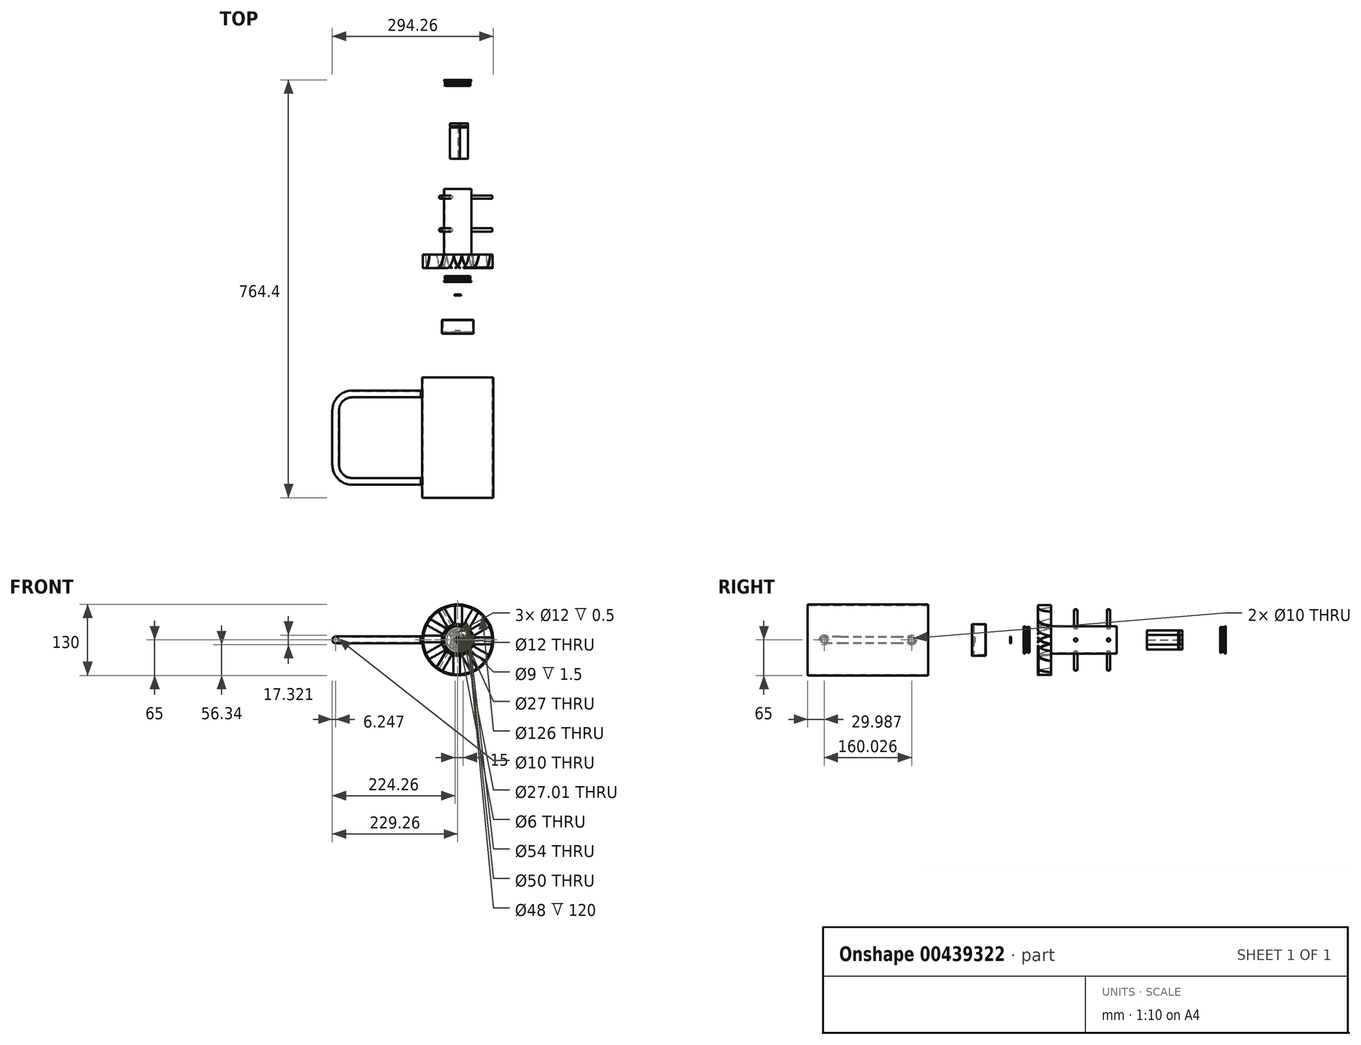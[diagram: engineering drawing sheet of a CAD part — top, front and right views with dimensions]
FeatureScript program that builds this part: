
annotation { "Feature Type Name" : "Feature", "Feature Type Description" : "" }
export const myFeature = defineFeature(function(context is Context, id is Id, definition is map)
    precondition{}
    {
        {
            var Q0;
            Q0=qCreatedBy(makeId("Right.planeOp"),FACE);
            var sketch = newSketch(context, id + "F0", { "sketchPlane" : qUnion([Q0])});
            skLineSegment(sketch, "E0", {"start": v(0, 0) * mm, "end": v(0, 5.8) * mm});
            skLineSegment(sketch, "E1", {"start": v(0.2, 6) * mm, "end": v(2, 6) * mm});
            skLineSegment(sketch, "E2", {"start": v(2, 6) * mm, "end": v(2, 4.31) * mm});
            skLineSegment(sketch, "E3", {"start": v(1.68, 3.67) * mm, "end": v(0.77, 3) * mm});
            skLineSegment(sketch, "E4", {"start": v(0.77, 3) * mm, "end": v(0.46, 3.46) * mm});
            skLineSegment(sketch, "E5", {"start": v(0.46, 3.46) * mm, "end": v(0.97, 4.13) * mm});
            skLineSegment(sketch, "E6", {"start": v(0.81, 4.53) * mm, "end": v(0, 4.66) * mm});
            skArc(sketch, "E7.filletArc", {"start": v(0.97, 4.13) * mm, "mid": v(1, 4.38) * mm, "end": v(0.81, 4.53) * mm});
            skPoint(sketch, "E8.visualSharp", {"position": v(0, 6) * mm});
            skArc(sketch, "E8.filletArc", {"start": v(0.2, 6) * mm, "mid": v(0.06, 5.94) * mm, "end": v(0, 5.8) * mm});
            skPoint(sketch, "E9.visualSharp", {"position": v(2, 3.9) * mm});
            skArc(sketch, "E9.filletArc", {"start": v(1.68, 3.67) * mm, "mid": v(1.91, 3.95) * mm, "end": v(2, 4.31) * mm});
            skLineSegment(sketch, "E10", {"start": v(-2.35, 0) * mm, "end": v(5.53, 0) * mm, "construction": true});
            skSolve(sketch);
        }
        {
            var Q0;
            Q0 = qSketchRegion(id + "F0", true);
            var Q1;
            Q1=sQuery(id+"F0.wireOp",EDGE,"E10");
            revolve(context, id + "F1", {"entities" : qUnion([Q0]), "axis" : qUnion([Q1]), "revolveType" : RevolveType.FULL});
        }
        {
            var Q0;
            Q0=makeQuery(id+"F1.opRevolve","SWEPT_BODY",BODY,{"disambiguationData":[OSD([sQuery(id+"F0.wireOp",EDGE,"E0"),sQuery(id+"F0.wireOp",EDGE,"E1"),sQuery(id+"F0.wireOp",EDGE,"E2"),sQuery(id+"F0.wireOp",EDGE,"E3"),sQuery(id+"F0.wireOp",EDGE,"E4"),sQuery(id+"F0.wireOp",EDGE,"E5"),sQuery(id+"F0.wireOp",EDGE,"E6"),sQuery(id+"F0.wireOp",EDGE,"E7.filletArc"),sQuery(id+"F0.wireOp",EDGE,"E8.filletArc"),sQuery(id+"F0.wireOp",EDGE,"E9.filletArc")])]});
            var Q1;
            Q1=makeQuery(id+"F1.opRevolve","SWEPT_FACE",FACE,{"disambiguationData":[OSD([sQuery(id+"F0.wireOp",EDGE,"E1")])]});
            transform(context, id + "F2", {"entities" : qUnion([Q0]), "transformType" : TransformType.TRANSLATION_DISTANCE, "transformDirection" : qUnion([Q1]), "distance" : 50 * mm, "makeCopy" : false});
        }
        {
            var Q0;
            Q0=qCreatedBy(makeId("Right.planeOp"),FACE);
            var sketch = newSketch(context, id + "F3", { "sketchPlane" : qUnion([Q0])});
            skLineSegment(sketch, "E11", {"start": v(0, 0) * mm, "end": v(0, 25) * mm});
            skLineSegment(sketch, "E12", {"start": v(0, 25) * mm, "end": v(2, 25) * mm});
            skLineSegment(sketch, "E13", {"start": v(2, 25) * mm, "end": v(2, 23.5) * mm});
            skLineSegment(sketch, "E14", {"start": v(2, 23.5) * mm, "end": v(4, 23.5) * mm});
            skLineSegment(sketch, "E15", {"start": v(4, 23.5) * mm, "end": v(4, 20) * mm});
            skLineSegment(sketch, "E16", {"start": v(4, 20) * mm, "end": v(7.5, 20) * mm});
            skLineSegment(sketch, "E17", {"start": v(7.5, 20) * mm, "end": v(7.5, 23.5) * mm});
            skLineSegment(sketch, "E18", {"start": v(7.5, 23.5) * mm, "end": v(10.5, 23.5) * mm});
            skLineSegment(sketch, "E19", {"start": v(10.5, 23.5) * mm, "end": v(10.5, 13.5) * mm});
            skLineSegment(sketch, "E20", {"start": v(10.5, 13.5) * mm, "end": v(4, 13.5) * mm});
            skLineSegment(sketch, "E21", {"start": v(4, 13.5) * mm, "end": v(4, 4.5) * mm});
            skLineSegment(sketch, "E22", {"start": v(4, 4.5) * mm, "end": v(2.5, 4.5) * mm});
            skLineSegment(sketch, "E23", {"start": v(2.5, 4.5) * mm, "end": v(2.5, 6) * mm});
            skLineSegment(sketch, "E24", {"start": v(2.5, 6) * mm, "end": v(0, 6) * mm});
            skLineSegment(sketch, "E25", {"start": v(-5.31, 0) * mm, "end": v(25.38, 0) * mm, "construction": true});
            skSolve(sketch);
        }
        {
            var Q0;
            Q0 = qSketchRegion(id + "F3", true);
            var Q1;
            Q1=sQuery(id+"F3.wireOp",EDGE,"E25");
            revolve(context, id + "F4", {"entities" : qUnion([Q0]), "axis" : qUnion([Q1]), "revolveType" : RevolveType.FULL});
        }
        {
            var Q0;
            Q0=makeQuery(id+"F4.opRevolve","SWEPT_EDGE",EDGE,{"disambiguationData":[OSD([sQuery(id+"F3.wireOp",EDGE,"E11"),sQuery(id+"F3.wireOp",EDGE,"E24")])]});
            chamfer(context, id + "F5", {"entities" : qUnion([Q0]), "chamferType" : ChamferType.OFFSET_ANGLE, "width" : .5 * mm, "oppositeDirection" : false, "angle" : 30 * degree, "tangentPropagation" : true});
        }
        {
            var Q0;
            Q0=makeQuery(id+"F4.opRevolve","SWEPT_EDGE",EDGE,{"disambiguationData":[OSD([sQuery(id+"F3.wireOp",EDGE,"E23"),sQuery(id+"F3.wireOp",EDGE,"E24")])]});
            var Q1;
            Q1=makeQuery(id+"F4.opRevolve","SWEPT_EDGE",EDGE,{"disambiguationData":[OSD([sQuery(id+"F3.wireOp",EDGE,"E17"),sQuery(id+"F3.wireOp",EDGE,"E18")])]});
            var Q2;
            Q2=makeQuery(id+"F4.opRevolve","SWEPT_EDGE",EDGE,{"disambiguationData":[OSD([sQuery(id+"F3.wireOp",EDGE,"E15"),sQuery(id+"F3.wireOp",EDGE,"E16")])]});
            var Q3;
            Q3=makeQuery(id+"F4.opRevolve","SWEPT_EDGE",EDGE,{"disambiguationData":[OSD([sQuery(id+"F3.wireOp",EDGE,"E20"),sQuery(id+"F3.wireOp",EDGE,"E21")])]});
            fillet(context, id + "F6", {"entities" : qUnion([Q0, Q1, Q2, Q3]), "radius" : .3 * mm, "tangentPropagation" : true, "allowEdgeOverflow" : false});
        }
        {
            var Q0;
            Q0=makeQuery(id+"F4.opRevolve","SWEPT_EDGE",EDGE,{"disambiguationData":[OSD([sQuery(id+"F3.wireOp",EDGE,"E11"),sQuery(id+"F3.wireOp",EDGE,"E12")])]});
            var Q1;
            Q1=makeQuery(id+"F4.opRevolve","SWEPT_EDGE",EDGE,{"disambiguationData":[OSD([sQuery(id+"F3.wireOp",EDGE,"E12"),sQuery(id+"F3.wireOp",EDGE,"E13")])]});
            var Q2;
            Q2=makeQuery(id+"F4.opRevolve","SWEPT_EDGE",EDGE,{"disambiguationData":[OSD([sQuery(id+"F3.wireOp",EDGE,"E14"),sQuery(id+"F3.wireOp",EDGE,"E15")])]});
            var Q3;
            Q3=makeQuery(id+"F4.opRevolve","SWEPT_EDGE",EDGE,{"disambiguationData":[OSD([sQuery(id+"F3.wireOp",EDGE,"E17"),sQuery(id+"F3.wireOp",EDGE,"E18")])]});
            var Q4;
            Q4=makeQuery(id+"F4.opRevolve","SWEPT_EDGE",EDGE,{"disambiguationData":[OSD([sQuery(id+"F3.wireOp",EDGE,"E18"),sQuery(id+"F3.wireOp",EDGE,"E19")])]});
            var Q5;
            Q5=makeQuery(id+"F4.opRevolve","SWEPT_EDGE",EDGE,{"disambiguationData":[OSD([sQuery(id+"F3.wireOp",EDGE,"E19"),sQuery(id+"F3.wireOp",EDGE,"E20")])]});
            chamfer(context, id + "F7", {"entities" : qUnion([Q0, Q1, Q2, Q3, Q4, Q5]), "width" : .5 * mm, "tangentPropagation" : true});
        }
        {
            var Q0;
            Q0=qCreatedBy(makeId("Right.planeOp"),FACE);
            var sketch = newSketch(context, id + "F8", { "sketchPlane" : qUnion([Q0])});
            skCircle(sketch, "E26", {"center": v(5.75, 21.75) * mm, "radius": 1.75 * mm});
            skLineSegment(sketch, "E27", {"start": v(-6.06, 0) * mm, "end": v(25.96, 0) * mm, "construction": true});
            skSolve(sketch);
        }
        {
            var Q0;
            Q0=makeQuery(id+"F8.imprint","IMPRINT",FACE,{"disambiguationData":[TD([[makeQuery(id+"F8.imprint","IMPRINT",EDGE,{"derivedFrom":sQuery(id+"F8.wireOp",EDGE,"E26")}),1.0]])]});
            var Q1;
            Q1=sQuery(id+"F8.wireOp",EDGE,"E27");
            revolve(context, id + "F9", {"operationType" : NewBodyOperationType.ADD, "entities" : qUnion([Q0]), "axis" : qUnion([Q1]), "revolveType" : RevolveType.FULL});
        }
        {
            var Q0;
            Q0=makeQuery(id+"F4.opRevolve","SWEPT_BODY",BODY,{"disambiguationData":[OSD([sQuery(id+"F3.wireOp",EDGE,"E11"),sQuery(id+"F3.wireOp",EDGE,"E12"),sQuery(id+"F3.wireOp",EDGE,"E13"),sQuery(id+"F3.wireOp",EDGE,"E14"),sQuery(id+"F3.wireOp",EDGE,"E15"),sQuery(id+"F3.wireOp",EDGE,"E16"),sQuery(id+"F3.wireOp",EDGE,"E17"),sQuery(id+"F3.wireOp",EDGE,"E18"),sQuery(id+"F3.wireOp",EDGE,"E19"),sQuery(id+"F3.wireOp",EDGE,"E20"),sQuery(id+"F3.wireOp",EDGE,"E21"),sQuery(id+"F3.wireOp",EDGE,"E22"),sQuery(id+"F3.wireOp",EDGE,"E23"),sQuery(id+"F3.wireOp",EDGE,"E24")])]});
            var Q1;
            Q1=makeQuery(id+"F9.opRevolve","SWEPT_BODY",BODY,{"disambiguationData":[OSD([sQuery(id+"F8.wireOp",EDGE,"E26")])]});
            var Q2;
            Q2=makeQuery(id+"F4.opRevolve","SWEPT_FACE",FACE,{"disambiguationData":[OSD([sQuery(id+"F3.wireOp",EDGE,"E18")])]});
            transform(context, id + "F10", {"entities" : qUnion([Q0, Q1]), "transformType" : TransformType.TRANSLATION_DISTANCE, "transformDirection" : qUnion([Q2]), "distance" : 25 * mm, "makeCopy" : false});
        }
        {
            var Q0;
            Q0=qCreatedBy(makeId("Right.planeOp"),FACE);
            var sketch = newSketch(context, id + "F11", { "sketchPlane" : qUnion([Q0])});
            skLineSegment(sketch, "E28", {"start": v(0, 3) * mm, "end": v(0, 5) * mm});
            skLineSegment(sketch, "E29", {"start": v(0, 5) * mm, "end": v(2, 5) * mm});
            skLineSegment(sketch, "E30", {"start": v(2, 5) * mm, "end": v(2, 25) * mm});
            skLineSegment(sketch, "E31", {"start": v(2, 25) * mm, "end": v(0, 25) * mm});
            skLineSegment(sketch, "E32", {"start": v(0, 25) * mm, "end": v(0, 29) * mm});
            skLineSegment(sketch, "E33", {"start": v(0, 29) * mm, "end": v(25.72, 29) * mm});
            skLineSegment(sketch, "E34", {"start": v(25.72, 29) * mm, "end": v(25.72, 27) * mm});
            skLineSegment(sketch, "E35", {"start": v(25.72, 27) * mm, "end": v(3.72, 27) * mm});
            skLineSegment(sketch, "E36", {"start": v(3.72, 27) * mm, "end": v(3.72, 5) * mm});
            skLineSegment(sketch, "E37", {"start": v(3.72, 5) * mm, "end": v(5.72, 5) * mm});
            skLineSegment(sketch, "E38", {"start": v(5.72, 5) * mm, "end": v(5.72, 3) * mm});
            skLineSegment(sketch, "E39", {"start": v(5.72, 3) * mm, "end": v(0, 3) * mm});
            skLineSegment(sketch, "E40", {"start": v(-6.87, 0) * mm, "end": v(43.92, 0) * mm, "construction": true});
            skSolve(sketch);
        }
        {
            var Q0;
            Q0 = qSketchRegion(id + "F11", true);
            var Q1;
            Q1=sQuery(id+"F11.wireOp",EDGE,"E40");
            revolve(context, id + "F12", {"entities" : qUnion([Q0]), "axis" : qUnion([Q1]), "revolveType" : RevolveType.FULL});
        }
        {
            var Q0;
            Q0=makeQuery(id+"F12.opRevolve","SWEPT_EDGE",EDGE,{"disambiguationData":[OSD([sQuery(id+"F11.wireOp",EDGE,"E28"),sQuery(id+"F11.wireOp",EDGE,"E39")])]});
            var Q1;
            Q1=makeQuery(id+"F12.opRevolve","SWEPT_EDGE",EDGE,{"disambiguationData":[OSD([sQuery(id+"F11.wireOp",EDGE,"E28"),sQuery(id+"F11.wireOp",EDGE,"E29")])]});
            var Q2;
            Q2=makeQuery(id+"F12.opRevolve","SWEPT_EDGE",EDGE,{"disambiguationData":[OSD([sQuery(id+"F11.wireOp",EDGE,"E31"),sQuery(id+"F11.wireOp",EDGE,"E32")])]});
            var Q3;
            Q3=makeQuery(id+"F12.opRevolve","SWEPT_EDGE",EDGE,{"disambiguationData":[OSD([sQuery(id+"F11.wireOp",EDGE,"E32"),sQuery(id+"F11.wireOp",EDGE,"E33")])]});
            var Q4;
            Q4=makeQuery(id+"F12.opRevolve","SWEPT_EDGE",EDGE,{"disambiguationData":[OSD([sQuery(id+"F11.wireOp",EDGE,"E33"),sQuery(id+"F11.wireOp",EDGE,"E34")])]});
            var Q5;
            Q5=makeQuery(id+"F12.opRevolve","SWEPT_EDGE",EDGE,{"disambiguationData":[OSD([sQuery(id+"F11.wireOp",EDGE,"E34"),sQuery(id+"F11.wireOp",EDGE,"E35")])]});
            var Q6;
            Q6=makeQuery(id+"F12.opRevolve","SWEPT_EDGE",EDGE,{"disambiguationData":[OSD([sQuery(id+"F11.wireOp",EDGE,"E37"),sQuery(id+"F11.wireOp",EDGE,"E38")])]});
            var Q7;
            Q7=makeQuery(id+"F12.opRevolve","SWEPT_EDGE",EDGE,{"disambiguationData":[OSD([sQuery(id+"F11.wireOp",EDGE,"E38"),sQuery(id+"F11.wireOp",EDGE,"E39")])]});
            chamfer(context, id + "F13", {"entities" : qUnion([Q0, Q1, Q2, Q3, Q4, Q5, Q6, Q7]), "width" : .5 * mm, "tangentPropagation" : true});
        }
        {
            var Q0;
            Q0=makeQuery(id+"F12.opRevolve","SWEPT_EDGE",EDGE,{"disambiguationData":[OSD([sQuery(id+"F11.wireOp",EDGE,"E29"),sQuery(id+"F11.wireOp",EDGE,"E30")])]});
            var Q1;
            Q1=makeQuery(id+"F12.opRevolve","SWEPT_EDGE",EDGE,{"disambiguationData":[OSD([sQuery(id+"F11.wireOp",EDGE,"E30"),sQuery(id+"F11.wireOp",EDGE,"E31")])]});
            var Q2;
            Q2=makeQuery(id+"F12.opRevolve","SWEPT_EDGE",EDGE,{"disambiguationData":[OSD([sQuery(id+"F11.wireOp",EDGE,"E35"),sQuery(id+"F11.wireOp",EDGE,"E36")])]});
            var Q3;
            Q3=makeQuery(id+"F12.opRevolve","SWEPT_EDGE",EDGE,{"disambiguationData":[OSD([sQuery(id+"F11.wireOp",EDGE,"E36"),sQuery(id+"F11.wireOp",EDGE,"E37")])]});
            fillet(context, id + "F14", {"entities" : qUnion([Q0, Q1, Q2, Q3]), "radius" : 1 * mm, "tangentPropagation" : true, "allowEdgeOverflow" : false});
        }
        {
            var Q0;
            Q0=qCreatedBy(makeId("Right.planeOp"),FACE);
            cPlane(context, id + "F15", {"entities" : qUnion([Q0]), "cplaneType" : CPlaneType.OFFSET, "offset" : 29 * mm, "width" : 150 * mm, "height" : 150 * mm});
        }
        {
            var Q0;
            Q0=qCreatedBy(id+"F15.planeOp",FACE);
            var sketch = newSketch(context, id + "F16", { "sketchPlane" : qUnion([Q0])});
            skFitSpline(sketch, "E41", {"points": [v(1.8, 4) * mm, v(0.76, 4.47) * mm, v(0.51, 3.63) * mm, v(0.79, 2.55) * mm, v(4.93, -1.3) * mm, v(11.9, -4.72) * mm, v(18.63, -6.73) * mm, v(25, -7.85) * mm], "startDerivative": vector(-10.22, 8.26) * mm, "endDerivative": vector(8.4, -0.71) * mm});
            skFitSpline(sketch, "E42", {"points": [v(25, -7.85) * mm, v(25.14, -7.8) * mm, v(24.7, -7.38) * mm, v(23.01, -6.96) * mm, v(19.16, -6.12) * mm, v(12.02, -3.74) * mm, v(5.67, -0.3) * mm, v(3.11, 2.55) * mm, v(1.8, 4) * mm], "startDerivative": vector(9.33, 0.6) * mm, "endDerivative": vector(-14.15, 14.4) * mm});
            skSolve(sketch);
        }
        {
            var Q0;
            Q0 = qSketchRegion(id + "F16", true);
            extrude(context, id + "F17", {"entities" : qUnion([Q0]), "depth" : 35 * mm, "hasSecondDirection" : true, "secondDirectionOppositeDirection" : true, "secondDirectionDepth" : 1.6 * mm});
        }
        {
            var Q0;
            Q0=makeQuery(id+"F12.opRevolve","SWEPT_BODY",BODY,{"disambiguationData":[OSD([sQuery(id+"F11.wireOp",EDGE,"E28"),sQuery(id+"F11.wireOp",EDGE,"E29"),sQuery(id+"F11.wireOp",EDGE,"E30"),sQuery(id+"F11.wireOp",EDGE,"E31"),sQuery(id+"F11.wireOp",EDGE,"E32"),sQuery(id+"F11.wireOp",EDGE,"E33"),sQuery(id+"F11.wireOp",EDGE,"E34"),sQuery(id+"F11.wireOp",EDGE,"E35"),sQuery(id+"F11.wireOp",EDGE,"E36"),sQuery(id+"F11.wireOp",EDGE,"E37"),sQuery(id+"F11.wireOp",EDGE,"E38"),sQuery(id+"F11.wireOp",EDGE,"E39")])]});
            var Q1;
            Q1=makeQuery(id+"F17.opExtrude","SWEPT_BODY",BODY,{"disambiguationData":[OSD([sQuery(id+"F16.wireOp",EDGE,"E41"),sQuery(id+"F16.wireOp",EDGE,"E42")])]});
            booleanBodies(context, id + "F18", {"operationType" : BooleanOperationType.SUBTRACTION, "tools" : qUnion([Q0]), "targets" : qUnion([Q1]), "keepTools" : true});
        }
        {
            var Q0;
            Q0=makeQuery(id+"F17.opExtrude","SWEPT_BODY",BODY,{"disambiguationData":[OSD([sQuery(id+"F16.wireOp",EDGE,"E41"),sQuery(id+"F16.wireOp",EDGE,"E42")])]});
            var Q1;
            Q1=makeQuery(id+"F12.opRevolve","SWEPT_FACE",FACE,{"disambiguationData":[OSD([sQuery(id+"F11.wireOp",EDGE,"E33")])]});
            circularPattern(context, id + "F19", {"entities" : qUnion([Q0]), "axis" : qUnion([Q1]), "angle" : 360 * degree, "instanceCount" : 12, "equalSpace" : true});
        }
        {
            var Q0;
            Q0=makeQuery(id+"F12.opRevolve","SWEPT_BODY",BODY,{"disambiguationData":[OSD([sQuery(id+"F11.wireOp",EDGE,"E28"),sQuery(id+"F11.wireOp",EDGE,"E29"),sQuery(id+"F11.wireOp",EDGE,"E30"),sQuery(id+"F11.wireOp",EDGE,"E31"),sQuery(id+"F11.wireOp",EDGE,"E32"),sQuery(id+"F11.wireOp",EDGE,"E33"),sQuery(id+"F11.wireOp",EDGE,"E34"),sQuery(id+"F11.wireOp",EDGE,"E35"),sQuery(id+"F11.wireOp",EDGE,"E36"),sQuery(id+"F11.wireOp",EDGE,"E37"),sQuery(id+"F11.wireOp",EDGE,"E38"),sQuery(id+"F11.wireOp",EDGE,"E39")])]});
            var Q1;
            Q1=makeQuery(id+"F4.opRevolve","SWEPT_FACE",FACE,{"disambiguationData":[OSD([sQuery(id+"F3.wireOp",EDGE,"E18")])]});
            transform(context, id + "F20", {"entities" : qUnion([Q0]), "transformType" : TransformType.TRANSLATION_DISTANCE, "transformDirection" : qUnion([Q1]), "distance" : 120 * mm, "makeCopy" : false});
        }
        {
            var Q0;
            Q0=qCreatedBy(makeId("Front.planeOp"),FACE);
            var sketch = newSketch(context, id + "F21", { "sketchPlane" : qUnion([Q0])});
            skCircle(sketch, "E43", {"center": v(0, 0) * mm, "radius": 65 * mm});
            skCircle(sketch, "E44", {"center": v(0, 0) * mm, "radius": 63 * mm});
            skSolve(sketch);
        }
        {
            var Q0;
            Q0 = qSketchRegion(id + "F21", true);
            extrude(context, id + "F22", {"entities" : qUnion([Q0]), "depth" : 220 * mm});
        }
        {
            var Q0;
            Q0=makeQuery(id+"F22.opExtrude","CAP_EDGE",EDGE,{"disambiguationData":[OSD([sQuery(id+"F21.wireOp",EDGE,"E43")])],"isStart":false});
            var Q1;
            Q1=makeQuery(id+"F22.opExtrude","CAP_EDGE",EDGE,{"disambiguationData":[OSD([sQuery(id+"F21.wireOp",EDGE,"E44")])],"isStart":false});
            var Q2;
            Q2=makeQuery(id+"F22.opExtrude","CAP_EDGE",EDGE,{"disambiguationData":[OSD([sQuery(id+"F21.wireOp",EDGE,"E43")])],"isStart":true});
            var Q3;
            Q3=makeQuery(id+"F22.opExtrude","CAP_EDGE",EDGE,{"disambiguationData":[OSD([sQuery(id+"F21.wireOp",EDGE,"E44")])],"isStart":true});
            fillet(context, id + "F23", {"entities" : qUnion([Q0, Q1, Q2, Q3]), "radius" : 1 * mm, "tangentPropagation" : true, "allowEdgeOverflow" : false});
        }
        {
            var Q0;
            Q0=makeQuery(id+"F22.opExtrude","SWEPT_BODY",BODY,{"disambiguationData":[OSD([sQuery(id+"F21.wireOp",EDGE,"E43"),sQuery(id+"F21.wireOp",EDGE,"E44")])]});
            var Q1;
            Q1=makeQuery(id+"F12.opRevolve","SWEPT_BODY",BODY,{"disambiguationData":[OSD([sQuery(id+"F11.wireOp",EDGE,"E28"),sQuery(id+"F11.wireOp",EDGE,"E29"),sQuery(id+"F11.wireOp",EDGE,"E30"),sQuery(id+"F11.wireOp",EDGE,"E31"),sQuery(id+"F11.wireOp",EDGE,"E32"),sQuery(id+"F11.wireOp",EDGE,"E33"),sQuery(id+"F11.wireOp",EDGE,"E34"),sQuery(id+"F11.wireOp",EDGE,"E35"),sQuery(id+"F11.wireOp",EDGE,"E36"),sQuery(id+"F11.wireOp",EDGE,"E37"),sQuery(id+"F11.wireOp",EDGE,"E38"),sQuery(id+"F11.wireOp",EDGE,"E39")])]});
            booleanBodies(context, id + "F24", {"operationType" : BooleanOperationType.SUBTRACTION, "tools" : qUnion([Q0]), "targets" : qUnion([Q1]), "keepTools" : true});
        }
        {
            var Q0;
            Q0=makeQuery(id+"F22.opExtrude","SWEPT_BODY",BODY,{"disambiguationData":[OSD([sQuery(id+"F21.wireOp",EDGE,"E43"),sQuery(id+"F21.wireOp",EDGE,"E44")])]});
            var Q1;
            Q1=makeQuery(id+"F22.opExtrude","SWEPT_FACE",FACE,{"disambiguationData":[OSD([sQuery(id+"F21.wireOp",EDGE,"E43")])]});
            transform(context, id + "F25", {"entities" : qUnion([Q0]), "transformType" : TransformType.TRANSLATION_DISTANCE, "transformDirection" : qUnion([Q1]), "distance" : 200 * mm, "oppositeDirection" : true, "makeCopy" : false});
        }
        {
            var Q0;
            Q0=qCreatedBy(makeId("Front.planeOp"),FACE);
            var sketch = newSketch(context, id + "F26", { "sketchPlane" : qUnion([Q0])});
            skCircle(sketch, "E45", {"center": v(0, 0) * mm, "radius": 25 * mm});
            skCircle(sketch, "E46", {"center": v(0, 0) * mm, "radius": 24 * mm});
            skSolve(sketch);
        }
        {
            var Q0;
            Q0 = qSketchRegion(id + "F26", true);
            extrude(context, id + "F27", {"entities" : qUnion([Q0]), "oppositeDirection" : true, "depth" : 120 * mm});
        }
        {
            var Q0;
            Q0=makeQuery(id+"F27.opExtrude","SWEPT_BODY",BODY,{"disambiguationData":[OSD([sQuery(id+"F26.wireOp",EDGE,"E45"),sQuery(id+"F26.wireOp",EDGE,"E46")])]});
            var Q1;
            Q1=makeQuery(id+"F27.opExtrude","SWEPT_FACE",FACE,{"disambiguationData":[OSD([sQuery(id+"F26.wireOp",EDGE,"E45")])]});
            transform(context, id + "F28", {"entities" : qUnion([Q0]), "transformType" : TransformType.TRANSLATION_DISTANCE, "transformDirection" : qUnion([Q1]), "distance" : 25 * mm, "oppositeDirection" : true, "makeCopy" : false});
        }
        {
            var Q0;
            Q0=qCreatedBy(id+"F15.planeOp",FACE);
            var sketch = newSketch(context, id + "F29", { "sketchPlane" : qUnion([Q0])});
            skCircle(sketch, "E47", {"center": v(0, 0) * mm, "radius": 3 * mm});
            skCircle(sketch, "E48", {"center": v(60, 0) * mm, "radius": 3 * mm});
            skSolve(sketch);
        }
        {
            var Q0;
            Q0 = qSketchRegion(id + "F29", true);
            extrude(context, id + "F30", {"entities" : qUnion([Q0]), "depth" : 34 * mm, "hasSecondDirection" : true, "secondDirectionOppositeDirection" : true, "secondDirectionDepth" : 4.5 * mm});
        }
        {
            var Q0;
            Q0=makeQuery(id+"F30.opExtrude","SWEPT_BODY",BODY,{"disambiguationData":[OSD([sQuery(id+"F29.wireOp",EDGE,"E47")])]});
            var Q1;
            Q1=makeQuery(id+"F30.opExtrude","SWEPT_BODY",BODY,{"disambiguationData":[OSD([sQuery(id+"F29.wireOp",EDGE,"E48")])]});
            var Q2;
            Q2=makeQuery(id+"F27.opExtrude","SWEPT_FACE",FACE,{"disambiguationData":[OSD([sQuery(id+"F26.wireOp",EDGE,"E45")])]});
            transform(context, id + "F31", {"entities" : qUnion([Q0, Q1]), "transformType" : TransformType.TRANSLATION_DISTANCE, "transformDirection" : qUnion([Q2]), "distance" : 70 * mm, "oppositeDirection" : true, "makeCopy" : false});
        }
        {
            var Q0;
            Q0=makeQuery(id+"F30.opExtrude","SWEPT_BODY",BODY,{"disambiguationData":[OSD([sQuery(id+"F29.wireOp",EDGE,"E47")])]});
            var Q1;
            Q1=makeQuery(id+"F30.opExtrude","SWEPT_BODY",BODY,{"disambiguationData":[OSD([sQuery(id+"F29.wireOp",EDGE,"E48")])]});
            var Q2;
            Q2=makeQuery(id+"F27.opExtrude","SWEPT_FACE",FACE,{"disambiguationData":[OSD([sQuery(id+"F26.wireOp",EDGE,"E45")])]});
            circularPattern(context, id + "F32", {"entities" : qUnion([Q0, Q1]), "axis" : qUnion([Q2]), "angle" : 360 * degree, "instanceCount" : 3, "equalSpace" : true});
        }
        {
            var Q0;
            Q0=makeQuery(id+"F27.opExtrude","SWEPT_BODY",BODY,{"disambiguationData":[OSD([sQuery(id+"F26.wireOp",EDGE,"E45"),sQuery(id+"F26.wireOp",EDGE,"E46")])]});
            var Q1;
            Q1=makeQuery(id+"F27.opExtrude","SWEPT_FACE",FACE,{"disambiguationData":[OSD([sQuery(id+"F26.wireOp",EDGE,"E45")])]});
            transform(context, id + "F33", {"entities" : qUnion([Q0]), "transformType" : TransformType.ROTATION, "transformAxis" : qUnion([Q1]), "angle" : 30 * degree, "oppositeDirection" : true, "makeCopy" : false});
        }
        {
            var Q0;
            Q0=qCreatedBy(makeId("Right.planeOp"),FACE);
            var sketch = newSketch(context, id + "F34", { "sketchPlane" : qUnion([Q0])});
            skLineSegment(sketch, "E49", {"start": v(0, 0) * mm, "end": v(30.7, 0) * mm, "construction": true});
            skLineSegment(sketch, "E50.MirrorCS", {"start": v(-16.1, 23.5) * mm, "end": v(-16.1, 13.5) * mm});
            skLineSegment(sketch, "E51.MirrorCS", {"start": v(-13.1, 23.5) * mm, "end": v(-16.1, 23.5) * mm});
            skLineSegment(sketch, "E52.MirrorCS", {"start": v(-13.1, 20) * mm, "end": v(-13.1, 23.5) * mm});
            skLineSegment(sketch, "E53.MirrorCS", {"start": v(-9.6, 13.5) * mm, "end": v(-9.6, 0) * mm});
            skLineSegment(sketch, "E54.MirrorCS", {"start": v(-9.6, 20) * mm, "end": v(-13.1, 20) * mm});
            skLineSegment(sketch, "E55.MirrorCS", {"start": v(-9.6, 23.5) * mm, "end": v(-9.6, 20) * mm});
            skLineSegment(sketch, "E56.MirrorCS", {"start": v(-7.6, 23.5) * mm, "end": v(-9.6, 23.5) * mm});
            skLineSegment(sketch, "E57.MirrorCS", {"start": v(-7.6, 25) * mm, "end": v(-7.6, 23.5) * mm});
            skLineSegment(sketch, "E58.MirrorCS", {"start": v(-5.6, 25) * mm, "end": v(-7.6, 25) * mm});
            skLineSegment(sketch, "E59.MirrorCS", {"start": v(-5.68, 0) * mm, "end": v(-5.6, 25) * mm});
            skLineSegment(sketch, "E60.MirrorCS", {"start": v(-16.1, 13.5) * mm, "end": v(-9.6, 13.5) * mm});
            skLineSegment(sketch, "E61.MirrorCS", {"start": v(-9.6, 0) * mm, "end": v(-5.68, 0) * mm});
            skSolve(sketch);
        }
        {
            var Q0;
            Q0 = qSketchRegion(id + "F34", true);
            var Q1;
            Q1=makeQuery(id+"F27.opExtrude","SWEPT_FACE",FACE,{"disambiguationData":[OSD([sQuery(id+"F26.wireOp",EDGE,"E45")])]});
            revolve(context, id + "F35", {"entities" : qUnion([Q0]), "axis" : qUnion([Q1]), "revolveType" : RevolveType.FULL});
        }
        {
            var Q0;
            Q0=makeQuery(id+"F35.opRevolve","SWEPT_BODY",BODY,{"disambiguationData":[OSD([sQuery(id+"F34.wireOp",EDGE,"E50.MirrorCS"),sQuery(id+"F34.wireOp",EDGE,"E51.MirrorCS"),sQuery(id+"F34.wireOp",EDGE,"E52.MirrorCS"),sQuery(id+"F34.wireOp",EDGE,"E53.MirrorCS"),sQuery(id+"F34.wireOp",EDGE,"E54.MirrorCS"),sQuery(id+"F34.wireOp",EDGE,"E55.MirrorCS"),sQuery(id+"F34.wireOp",EDGE,"E56.MirrorCS"),sQuery(id+"F34.wireOp",EDGE,"E57.MirrorCS"),sQuery(id+"F34.wireOp",EDGE,"E58.MirrorCS"),sQuery(id+"F34.wireOp",EDGE,"E59.MirrorCS"),sQuery(id+"F34.wireOp",EDGE,"E60.MirrorCS"),sQuery(id+"F34.wireOp",EDGE,"E61.MirrorCS")])]});
            var Q1;
            Q1=makeQuery(id+"F27.opExtrude","SWEPT_FACE",FACE,{"disambiguationData":[OSD([sQuery(id+"F26.wireOp",EDGE,"E45")])]});
            transform(context, id + "F36", {"entities" : qUnion([Q0]), "transformType" : TransformType.TRANSLATION_DISTANCE, "transformDirection" : qUnion([Q1]), "distance" : 350 * mm, "oppositeDirection" : true, "makeCopy" : false});
        }
        {
            var Q0;
            Q0=makeQuery(id+"F35.opRevolve","SWEPT_EDGE",EDGE,{"disambiguationData":[OSD([sQuery(id+"F34.wireOp",EDGE,"E50.MirrorCS"),sQuery(id+"F34.wireOp",EDGE,"E51.MirrorCS")])]});
            var Q1;
            Q1=makeQuery(id+"F35.opRevolve","SWEPT_EDGE",EDGE,{"disambiguationData":[OSD([sQuery(id+"F34.wireOp",EDGE,"E51.MirrorCS"),sQuery(id+"F34.wireOp",EDGE,"E52.MirrorCS")])]});
            var Q2;
            Q2=makeQuery(id+"F35.opRevolve","SWEPT_EDGE",EDGE,{"disambiguationData":[OSD([sQuery(id+"F34.wireOp",EDGE,"E57.MirrorCS"),sQuery(id+"F34.wireOp",EDGE,"E58.MirrorCS")])]});
            var Q3;
            Q3=makeQuery(id+"F35.opRevolve","SWEPT_EDGE",EDGE,{"disambiguationData":[OSD([sQuery(id+"F34.wireOp",EDGE,"E58.MirrorCS"),sQuery(id+"F34.wireOp",EDGE,"E59.MirrorCS")])]});
            var Q4;
            Q4=makeQuery(id+"F35.opRevolve","SWEPT_EDGE",EDGE,{"disambiguationData":[OSD([sQuery(id+"F34.wireOp",EDGE,"E50.MirrorCS"),sQuery(id+"F34.wireOp",EDGE,"E60.MirrorCS")])]});
            chamfer(context, id + "F37", {"entities" : qUnion([Q0, Q1, Q2, Q3, Q4]), "width" : .5 * mm, "tangentPropagation" : true});
        }
        {
            var Q0;
            Q0=makeQuery(id+"F35.opRevolve","SWEPT_EDGE",EDGE,{"disambiguationData":[OSD([sQuery(id+"F34.wireOp",EDGE,"E53.MirrorCS"),sQuery(id+"F34.wireOp",EDGE,"E60.MirrorCS")])]});
            var Q1;
            Q1=makeQuery(id+"F35.opRevolve","SWEPT_EDGE",EDGE,{"disambiguationData":[OSD([sQuery(id+"F34.wireOp",EDGE,"E54.MirrorCS"),sQuery(id+"F34.wireOp",EDGE,"E55.MirrorCS")])]});
            var Q2;
            Q2=makeQuery(id+"F35.opRevolve","SWEPT_EDGE",EDGE,{"disambiguationData":[OSD([sQuery(id+"F34.wireOp",EDGE,"E52.MirrorCS"),sQuery(id+"F34.wireOp",EDGE,"E54.MirrorCS")])]});
            fillet(context, id + "F38", {"entities" : qUnion([Q0, Q1, Q2]), "radius" : .5 * mm, "tangentPropagation" : true, "allowEdgeOverflow" : false});
        }
        {
            var Q0;
            Q0=makeQuery(id+"F9.opRevolve","SWEPT_BODY",BODY,{"disambiguationData":[OSD([sQuery(id+"F8.wireOp",EDGE,"E26")])]});
            var Q1;
            Q1=makeQuery(id+"F27.opExtrude","SWEPT_FACE",FACE,{"disambiguationData":[OSD([sQuery(id+"F26.wireOp",EDGE,"E45")])]});
            transform(context, id + "F39", {"entities" : qUnion([Q0]), "transformType" : TransformType.TRANSLATION_DISTANCE, "transformDirection" : qUnion([Q1]), "distance" : 357.9 * mm, "oppositeDirection" : true, "makeCopy" : true});
        }
        {
            var Q0;
            Q0=qCreatedBy(makeId("Right.planeOp"),FACE);
            var sketch = newSketch(context, id + "F40", { "sketchPlane" : qUnion([Q0])});
            skLineSegment(sketch, "E62", {"start": v(0, 0) * mm, "end": v(0, 9) * mm});
            skLineSegment(sketch, "E63", {"start": v(0, 9) * mm, "end": v(57.5, 9) * mm});
            skLineSegment(sketch, "E64", {"start": v(57.5, 9) * mm, "end": v(57.5, 8.7) * mm});
            skLineSegment(sketch, "E65", {"start": v(57.5, 8.7) * mm, "end": v(60, 8.7) * mm});
            skLineSegment(sketch, "E66", {"start": v(60, 8.7) * mm, "end": v(60, 9) * mm});
            skLineSegment(sketch, "E67", {"start": v(60, 9) * mm, "end": v(65, 9) * mm});
            skLineSegment(sketch, "E68", {"start": v(65, 0) * mm, "end": v(0, 0) * mm});
            skLineSegment(sketch, "E69", {"start": v(65, 9) * mm, "end": v(65, 6) * mm});
            skLineSegment(sketch, "E70", {"start": v(65, 6) * mm, "end": v(64.5, 6) * mm});
            skLineSegment(sketch, "E71", {"start": v(64.5, 6) * mm, "end": v(64.5, 4) * mm});
            skLineSegment(sketch, "E72", {"start": v(64.5, 4) * mm, "end": v(65, 4) * mm});
            skLineSegment(sketch, "E73", {"start": v(65, 4) * mm, "end": v(65, 0) * mm});
            skSolve(sketch);
        }
        {
            var Q0;
            Q0 = qSketchRegion(id + "F40", true);
            var Q1;
            Q1=makeQuery(id+"F4.opRevolve","SWEPT_FACE",FACE,{"disambiguationData":[OSD([sQuery(id+"F3.wireOp",EDGE,"E18")])]});
            revolve(context, id + "F41", {"entities" : qUnion([Q0]), "axis" : qUnion([Q1]), "revolveType" : RevolveType.FULL});
        }
        {
            var Q0;
            Q0=makeQuery(id+"F41.opRevolve","SWEPT_BODY",BODY,{"disambiguationData":[OSD([sQuery(id+"F40.wireOp",EDGE,"E62"),sQuery(id+"F40.wireOp",EDGE,"E63"),sQuery(id+"F40.wireOp",EDGE,"E64"),sQuery(id+"F40.wireOp",EDGE,"E65"),sQuery(id+"F40.wireOp",EDGE,"E66"),sQuery(id+"F40.wireOp",EDGE,"E67"),sQuery(id+"F40.wireOp",EDGE,"Y38QIK3i-MWIf-Q0gZ-pP8j-5flM68i2H9gC"),sQuery(id+"F40.wireOp",EDGE,"E68")])]});
            var Q1;
            Q1=makeQuery(id+"F27.opExtrude","SWEPT_FACE",FACE,{"disambiguationData":[OSD([sQuery(id+"F26.wireOp",EDGE,"E45")])]});
            transform(context, id + "F42", {"entities" : qUnion([Q0]), "transformType" : TransformType.TRANSLATION_DISTANCE, "transformDirection" : qUnion([Q1]), "distance" : 200 * mm, "oppositeDirection" : true, "makeCopy" : false});
        }
        {
            var Q0;
            Q0=makeQuery(id+"F41.opRevolve","SWEPT_EDGE",EDGE,{"disambiguationData":[OSD([sQuery(id+"F40.wireOp",EDGE,"E62"),sQuery(id+"F40.wireOp",EDGE,"E63")])]});
            var Q1;
            Q1=makeQuery(id+"F41.opRevolve","SWEPT_EDGE",EDGE,{"disambiguationData":[OSD([sQuery(id+"F40.wireOp",EDGE,"E67"),sQuery(id+"F40.wireOp",EDGE,"Y38QIK3i-MWIf-Q0gZ-pP8j-5flM68i2H9gC")])]});
            fillet(context, id + "F43", {"entities" : qUnion([Q0, Q1]), "radius" : 1 * mm, "tangentPropagation" : true, "allowEdgeOverflow" : false});
        }
        {
            var Q0;
            Q0=makeQuery(id+"F41.opRevolve","SWEPT_EDGE",EDGE,{"disambiguationData":[OSD([sQuery(id+"F40.wireOp",EDGE,"E65"),sQuery(id+"F40.wireOp",EDGE,"E66")])]});
            var Q1;
            Q1=makeQuery(id+"F41.opRevolve","SWEPT_EDGE",EDGE,{"disambiguationData":[OSD([sQuery(id+"F40.wireOp",EDGE,"E64"),sQuery(id+"F40.wireOp",EDGE,"E65")])]});
            var Q2;
            Q2=makeQuery(id+"F41.opRevolve","SWEPT_EDGE",EDGE,{"disambiguationData":[OSD([sQuery(id+"F40.wireOp",EDGE,"E72"),sQuery(id+"F40.wireOp",EDGE,"E73")])]});
            fillet(context, id + "F44", {"entities" : qUnion([Q0, Q1, Q2]), "radius" : .5 * mm, "tangentPropagation" : true, "allowEdgeOverflow" : false});
        }
        {
            var Q0;
            Q0=makeQuery(id+"F41.opRevolve","SWEPT_BODY",BODY,{"disambiguationData":[OSD([sQuery(id+"F40.wireOp",EDGE,"E62"),sQuery(id+"F40.wireOp",EDGE,"E63"),sQuery(id+"F40.wireOp",EDGE,"E64"),sQuery(id+"F40.wireOp",EDGE,"E65"),sQuery(id+"F40.wireOp",EDGE,"E66"),sQuery(id+"F40.wireOp",EDGE,"E67"),sQuery(id+"F40.wireOp",EDGE,"Y38QIK3i-MWIf-Q0gZ-pP8j-5flM68i2H9gC"),sQuery(id+"F40.wireOp",EDGE,"E68")])]});
            transform(context, id + "F45", {"entities" : qUnion([Q0]), "transformType" : TransformType.TRANSLATION_3D, "dx" : 10 * mm, "dy" : 0 * mm, "dz" : 0 * mm, "makeCopy" : false});
        }
        {
            var Q0;
            Q0=makeQuery(id+"F41.opRevolve","SWEPT_BODY",BODY,{"disambiguationData":[OSD([sQuery(id+"F40.wireOp",EDGE,"E62"),sQuery(id+"F40.wireOp",EDGE,"E63"),sQuery(id+"F40.wireOp",EDGE,"E64"),sQuery(id+"F40.wireOp",EDGE,"E65"),sQuery(id+"F40.wireOp",EDGE,"E66"),sQuery(id+"F40.wireOp",EDGE,"E67"),sQuery(id+"F40.wireOp",EDGE,"Y38QIK3i-MWIf-Q0gZ-pP8j-5flM68i2H9gC"),sQuery(id+"F40.wireOp",EDGE,"E68")])]});
            var Q1;
            Q1=makeQuery(id+"F27.opExtrude","SWEPT_FACE",FACE,{"disambiguationData":[OSD([sQuery(id+"F26.wireOp",EDGE,"E45")])]});
            circularPattern(context, id + "F46", {"entities" : qUnion([Q0]), "axis" : qUnion([Q1]), "angle" : 360 * degree, "instanceCount" : 3, "equalSpace" : true});
        }
        {
            var Q0;
            Q0 = qSketchRegion(id + "F40", true);
            var Q1;
            Q1=makeQuery(id+"F27.opExtrude","SWEPT_FACE",FACE,{"disambiguationData":[OSD([sQuery(id+"F26.wireOp",EDGE,"E45")])]});
            revolve(context, id + "F47", {"entities" : qUnion([Q0]), "axis" : qUnion([Q1]), "revolveType" : RevolveType.FULL});
        }
        {
            var Q0;
            Q0=makeQuery(id+"F47.opRevolve","SWEPT_BODY",BODY,{"disambiguationData":[OSD([sQuery(id+"F40.wireOp",EDGE,"E62"),sQuery(id+"F40.wireOp",EDGE,"E63"),sQuery(id+"F40.wireOp",EDGE,"E64"),sQuery(id+"F40.wireOp",EDGE,"E65"),sQuery(id+"F40.wireOp",EDGE,"E66"),sQuery(id+"F40.wireOp",EDGE,"E67"),sQuery(id+"F40.wireOp",EDGE,"E68"),sQuery(id+"F40.wireOp",EDGE,"E69"),sQuery(id+"F40.wireOp",EDGE,"E70"),sQuery(id+"F40.wireOp",EDGE,"E71"),sQuery(id+"F40.wireOp",EDGE,"E72"),sQuery(id+"F40.wireOp",EDGE,"E73")])]});
            deleteBodies(context, id + "F48", {"entities" : qUnion([Q0])});
        }
        {
            var Q0;
            Q0=qCreatedBy(makeId("Top.planeOp"),FACE);
            var sketch = newSketch(context, id + "F49", { "sketchPlane" : qUnion([Q0])});
            skLineSegment(sketch, "E74", {"start": v(-63, -390) * mm, "end": v(-193, -390) * mm});
            skLineSegment(sketch, "E75", {"start": v(-223, -360) * mm, "end": v(-223, -260) * mm});
            skLineSegment(sketch, "E76", {"start": v(-193, -230) * mm, "end": v(-63, -230) * mm});
            skPoint(sketch, "E77.visualSharp", {"position": v(-223, -390) * mm});
            skArc(sketch, "E77.filletArc", {"start": v(-223, -360) * mm, "mid": v(-217.37, -377.5) * mm, "end": v(-202.58, -388.43) * mm});
            skPoint(sketch, "E78.visualSharp", {"position": v(-223, -230) * mm});
            skArc(sketch, "E78.filletArc", {"start": v(-193, -230) * mm, "mid": v(-209.96, -235.25) * mm, "end": v(-220.98, -249.17) * mm});
            skPoint(sketch, "E79.visualSharp", {"position": v(-193, -390) * mm});
            skArc(sketch, "E79.filletArc", {"start": v(-202.58, -388.43) * mm, "mid": v(-197.85, -389.6) * mm, "end": v(-193, -390) * mm});
            skPoint(sketch, "E80.visualSharp", {"position": v(-223, -260) * mm});
            skArc(sketch, "E80.filletArc", {"start": v(-220.98, -249.17) * mm, "mid": v(-222.5, -254.5) * mm, "end": v(-223, -260) * mm});
            skSolve(sketch);
        }
        {
            var Q0;
            Q0=qCreatedBy(makeId("Right.planeOp"),FACE);
            cPlane(context, id + "F50", {"entities" : qUnion([Q0]), "cplaneType" : CPlaneType.OFFSET, "offset" : 63 * mm, "oppositeDirection" : true, "width" : 150 * mm, "height" : 150 * mm});
        }
        {
            var Q0;
            Q0=qCreatedBy(id+"F50.planeOp",FACE);
            var sketch = newSketch(context, id + "F51", { "sketchPlane" : qUnion([Q0])});
            skCircle(sketch, "E81", {"center": v(-390.01, 0) * mm, "radius": 6.25 * mm});
            skCircle(sketch, "E82", {"center": v(-390.01, 0) * mm, "radius": 5 * mm});
            skSolve(sketch);
        }
        {
            var Q0;
            Q0 = qSketchRegion(id + "F51", true);
            var Q1;
            Q1 = qConstructionFilter(qBodyType(qCreatedBy(id + "F49" ,EDGE), BodyType.WIRE), ConstructionObject.NO);
            sweep(context, id + "F52", {"operationType" : NewBodyOperationType.ADD, "profiles" : qUnion([Q0]), "path" : qUnion([Q1])});
        }
        {
            var Q0;
            Q0 = qSketchRegion(id + "F51", true);
            var Q1;
            Q1 = qConstructionFilter(qBodyType(qCreatedBy(id + "F49" ,EDGE), BodyType.WIRE), ConstructionObject.NO);
            sweep(context, id + "F53", {"operationType" : NewBodyOperationType.ADD, "profiles" : qUnion([Q0]), "path" : qUnion([Q1])});
        }
        {
            var Q0;
            Q0=makeQuery(id+"F52.boolean.opBoolean","INTERSECT",EDGE,{"derivedFrom":[makeQuery(id+"F22.opExtrude","SWEPT_FACE",FACE,{"disambiguationData":[OSD([sQuery(id+"F21.wireOp",EDGE,"E43")])]}),makeQuery(id+"F52.opSweep","SWEPT_FACE",FACE,{"disambiguationData":[OSD([sQuery(id+"F49.wireOp",EDGE,"E76"),sQuery(id+"F51.wireOp",EDGE,"E81")])]})]});
            var Q1;
            Q1=makeQuery(id+"F52.boolean.opBoolean","INTERSECT",EDGE,{"derivedFrom":[makeQuery(id+"F22.opExtrude","SWEPT_FACE",FACE,{"disambiguationData":[OSD([sQuery(id+"F21.wireOp",EDGE,"E43")])]}),makeQuery(id+"F52.opSweep","SWEPT_FACE",FACE,{"disambiguationData":[OSD([sQuery(id+"F49.wireOp",EDGE,"E74"),sQuery(id+"F51.wireOp",EDGE,"E81")])]})]});
            fillet(context, id + "F54", {"entities" : qUnion([Q0, Q1]), "radius" : 3 * mm, "tangentPropagation" : true, "allowEdgeOverflow" : false});
        }
    });
